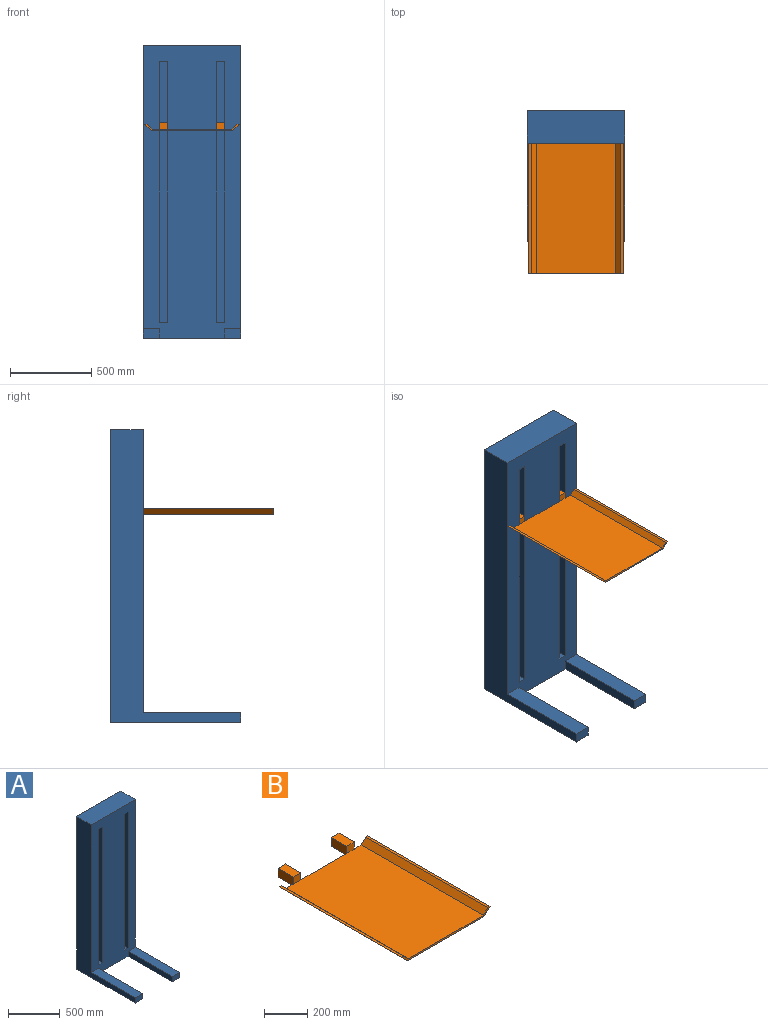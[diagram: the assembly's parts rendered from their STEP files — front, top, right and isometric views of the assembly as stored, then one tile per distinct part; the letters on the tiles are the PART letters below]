
ASSEMBLY  parts=2 mates=1
PART A: 22 faces, bbox 600x800x1800 mm
  f0: plane 1800x600mm, normal (0,-1,0), area 908000mm2, adj f1,f2,f3,f4,f6,f7,f9,f10
  f1: plane 1800x800mm, normal (-1,0,0), area 396000mm2, adj f0,f2,f4,f5,f6,f8
  f2: plane 800x600mm, normal (0,0,-1), area 240000mm2, adj f0,f1,f3,f5,f7,f8,f10,f11
  f3: plane 1800x800mm, normal (1,0,0), area 396000mm2, adj f0,f2,f4,f5,f9,f11
  f4: plane 600x200mm, normal (0,0,1), area 120000mm2, adj f0,f1,f3,f5
  f5: plane 1800x600mm, normal (0,1,0), area 1080000mm2, adj f1,f2,f3,f4
  f6: plane 600x100mm, normal (0,0,1), area 60000mm2, adj f0,f1,f7,f8
  f7: plane 600x60mm, normal (1,0,0), area 36000mm2, adj f0,f2,f6,f8
  f8: plane 100x60mm, normal (0,-1,0), area 6000mm2, adj f1,f2,f6,f7
  f9: plane 600x100mm, normal (0,0,1), area 60000mm2, adj f0,f3,f10,f11
  f10: plane 600x60mm, normal (-1,0,0), area 36000mm2, adj f0,f2,f9,f11
  f11: plane 100x60mm, normal (0,-1,0), area 6000mm2, adj f2,f3,f9,f10
  f12: plane 1600x100mm, normal (-1,0,0), area 160000mm2, adj f0,f13,f15,f16
  f13: plane 100x50mm, normal (0,0,-1), area 5000mm2, adj f0,f12,f14,f16
  f14: plane 1600x100mm, normal (1,0,0), area 160000mm2, adj f0,f13,f15,f16
  f15: plane 100x50mm, normal (0,0,1), area 5000mm2, adj f0,f12,f14,f16
  f16: plane 1600x50mm, normal (0,-1,0), area 80000mm2, adj f12,f13,f14,f15
  f17: plane 100x50mm, normal (0,0,-1), area 5000mm2, adj f0,f18,f20,f21
  f18: plane 1600x100mm, normal (1,0,0), area 160000mm2, adj f0,f17,f19,f21
  f19: plane 100x50mm, normal (0,0,1), area 5000mm2, adj f0,f18,f20,f21
  f20: plane 1600x100mm, normal (-1,0,0), area 160000mm2, adj f0,f17,f19,f21
  f21: plane 1600x50mm, normal (0,-1,0), area 80000mm2, adj f17,f18,f19,f20
PART B: 24 faces, bbox 580.2x900x50 mm
  f0: plane 300x10mm, normal (0,1,0), area 3000.2mm2, adj f2,f6,f14,f20
  f1: plane 90.08x40.1mm, normal (0,1,0), area 975.5mm2, adj f2,f6,f7,f8,f9,f12
  f2: plane 800x491.72mm, normal (0,0,1), area 393372.6mm2, adj f0,f1,f3,f9,f10,f11,f17,f23
  f3: plane 800x30.1mm, normal (0.71,0,0.71), area 34050.9mm2, adj f2,f4,f10,f11
  f4: plane 800x14.12mm, normal (0,0,1), area 11296.2mm2, adj f3,f5,f10,f11
  f5: plane 800x40.08mm, normal (-0.71,0,-0.71), area 45339.9mm2, adj f4,f6,f10,f11
  f6: plane 800x500mm, normal (0,0,-1), area 400000mm2, adj f0,f1,f5,f7,f10,f11,f15,f19
  f7: plane 800x40.08mm, normal (0.71,0,-0.71), area 45339.9mm2, adj f1,f6,f8,f10
  f8: plane 800x14.12mm, normal (0,0,1), area 11296.2mm2, adj f1,f7,f9,f10
  f9: plane 800x30.1mm, normal (-0.71,0,0.71), area 34050.9mm2, adj f1,f2,f8,f10
  f10: plane 580.15x40.1mm, normal (0,-1,0), area 5951mm2, adj f2,f3,f4,f5,f6,f7,f8,f9
  f11: plane 90.08x40.1mm, normal (0,1,0), area 975.5mm2, adj f2,f3,f4,f5,f6,f18
  f12: plane 100x50mm, normal (1,0,0), area 5000mm2, adj f1,f13,f15,f16,f17
  f13: plane 100x50mm, normal (0,0,1), area 5000mm2, adj f12,f14,f16,f17
  f14: plane 100x50mm, normal (-1,0,0), area 5000mm2, adj f0,f13,f15,f16,f17
  f15: plane 100x50mm, normal (0,0,-1), area 5000mm2, adj f6,f12,f14,f16
  f16: plane 50x50mm, normal (0,1,0), area 2500mm2, adj f12,f13,f14,f15
  f17: plane 50x40mm, normal (0,-1,0), area 1999.9mm2, adj f2,f12,f13,f14
  f18: plane 100x50mm, normal (-1,0,0), area 5000mm2, adj f11,f19,f21,f22,f23
  f19: plane 100x50mm, normal (0,0,-1), area 5000mm2, adj f6,f18,f20,f22
  f20: plane 100x50mm, normal (1,0,0), area 5000mm2, adj f0,f19,f21,f22,f23
  f21: plane 100x50mm, normal (0,0,1), area 5000mm2, adj f18,f20,f22,f23
  f22: plane 50x50mm, normal (0,1,0), area 2500mm2, adj f18,f19,f20,f21
  f23: plane 50x40mm, normal (0,-1,0), area 1999.9mm2, adj f2,f18,f20,f21
PLACE A t=(-1378.49,312.61,-297.37)mm
PLACE B t=(-116.43,-135.64,618.14)mm
MATE parallel B.f21 <-> A.f17  axis (0,0,1) through (-1253.49,162.61,1029.25)mm
